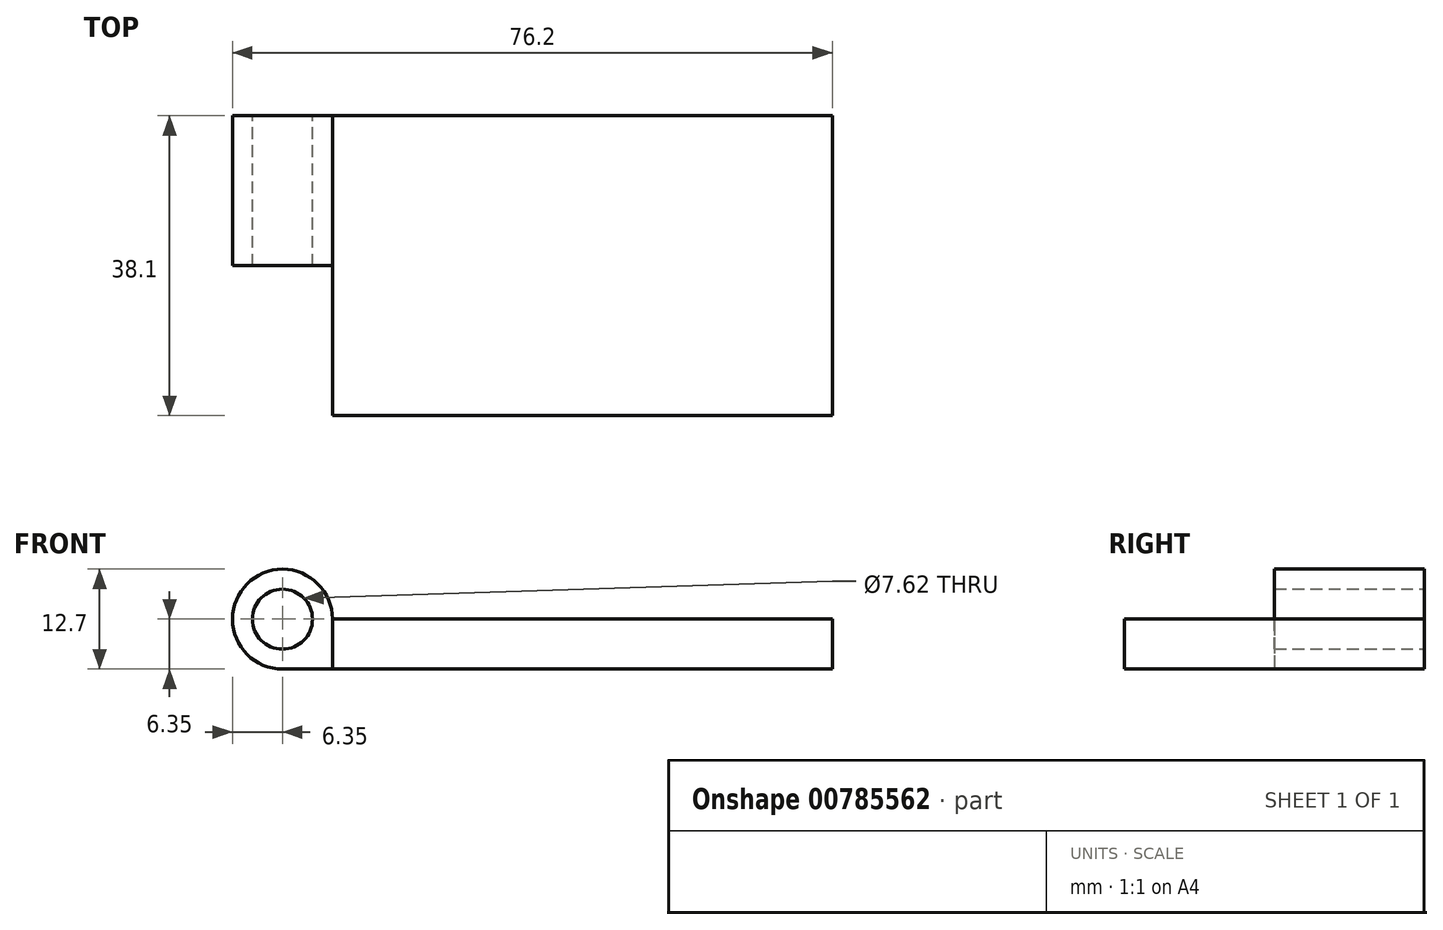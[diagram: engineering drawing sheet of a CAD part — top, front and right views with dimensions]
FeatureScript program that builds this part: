
annotation { "Feature Type Name" : "Feature", "Feature Type Description" : "" }
export const myFeature = defineFeature(function(context is Context, id is Id, definition is map)
    precondition{}
    {
        {
            var Q0;
            Q0=qCreatedBy(makeId("Front.planeOp"),FACE);
            var sketch = newSketch(context, id + "F0", { "sketchPlane" : qUnion([Q0])});
            skLineSegment(sketch, "E0.top", {"start": v(38.1, -6.35) * mm, "end": v(-31.75, -6.35) * mm});
            skLineSegment(sketch, "E0.left", {"start": v(38.1, 0) * mm, "end": v(38.1, -6.35) * mm});
            skPoint(sketch, "E0.middle", {"position": v(0, 0) * mm});
            skLineSegment(sketch, "E1.top", {"start": v(38.1, 0) * mm, "end": v(-25.4, 0) * mm});
            skLineSegment(sketch, "E2", {"start": v(-25.4, 0) * mm, "end": v(-31.75, 0) * mm});
            skCircle(sketch, "E3", {"center": v(-31.75, 0) * mm, "radius": 6.35 * mm});
            skPoint(sketch, "E4.orphan", {"position": v(-38.1, 6.35) * mm});
            skPoint(sketch, "E5.orphan", {"position": v(-38.1, -6.35) * mm});
            skPoint(sketch, "E6.orphan", {"position": v(38.1, 6.35) * mm});
            skCircle(sketch, "E7", {"center": v(-31.75, 0) * mm, "radius": 3.81 * mm});
            skSolve(sketch);
        }
        {
            var Q0;
            Q0 = qSketchRegion(id + "F0", true);
            extrude(context, id + "F1", {"entities" : qUnion([Q0]), "depth" : 38.1 * mm, "offsetDistance" : 25.4 * mm});
        }
        {
            var Q0;
            Q0=makeQuery(id+"F1.opExtrude","CAP_FACE",FACE,{"disambiguationData":[OSD([sQuery(id+"F0.wireOp",EDGE,"E0.top"),sQuery(id+"F0.wireOp",EDGE,"E0.left"),sQuery(id+"F0.wireOp",EDGE,"E1.top"),sQuery(id+"F0.wireOp",EDGE,"E3"),sQuery(id+"F0.wireOp",EDGE,"E7")])],"isStart":false});
            var sketch = newSketch(context, id + "F2", { "sketchPlane" : qUnion([Q0])});
            skArc(sketch, "E8", {"start": v(-25.4, 0) * mm, "mid": v(-36.24, 4.5) * mm, "end": v(-31.75, -6.35) * mm});
            skLineSegment(sketch, "E9", {"start": v(-25.4, 0) * mm, "end": v(-25.4, -6.35) * mm});
            skLineSegment(sketch, "E10", {"start": v(-25.4, -6.35) * mm, "end": v(-31.75, -6.35) * mm});
            skSolve(sketch);
        }
        {
            var Q0;
            Q0 = qSketchRegion(id + "F2", true);
            extrude(context, id + "F3", {"entities" : qUnion([Q0]), "operationType" : NewBodyOperationType.REMOVE, "oppositeDirection" : true, "depth" : 19.05 * mm, "offsetDistance" : 25.4 * mm});
        }
    });
